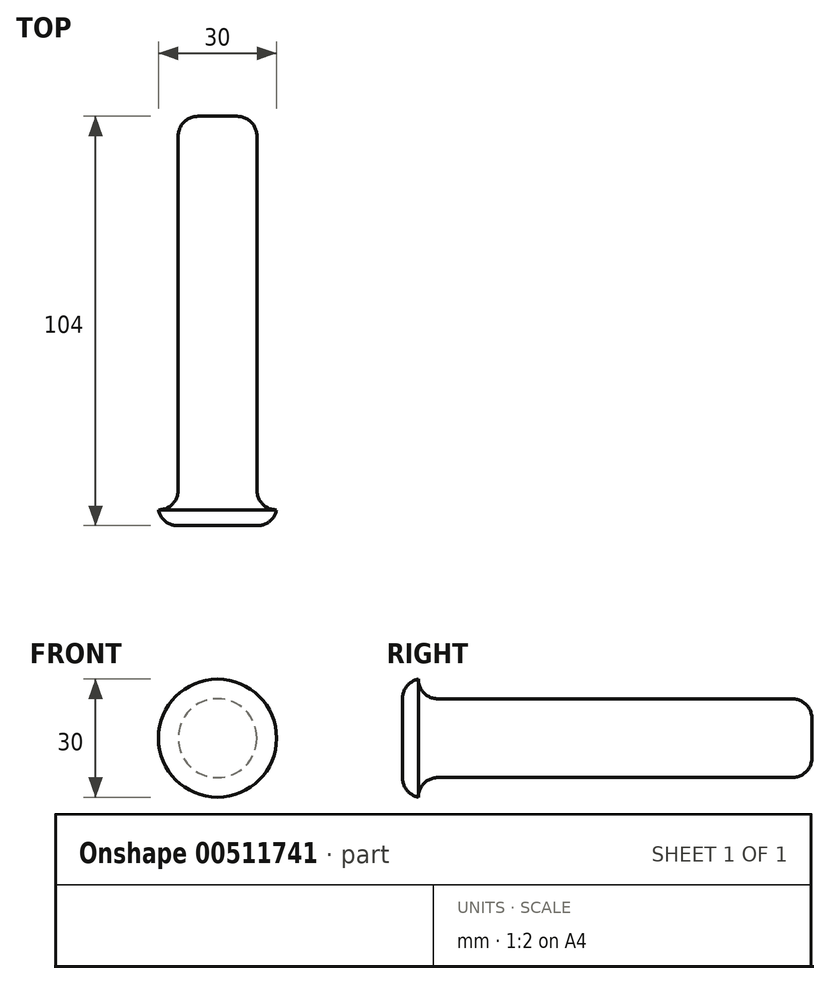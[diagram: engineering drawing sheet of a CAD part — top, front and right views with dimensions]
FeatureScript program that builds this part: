
annotation { "Feature Type Name" : "Feature", "Feature Type Description" : "" }
export const myFeature = defineFeature(function(context is Context, id is Id, definition is map)
    precondition{}
    {
        {
            var Q0;
            Q0=qCreatedBy(makeId("Front.planeOp"),FACE);
            var sketch = newSketch(context, id + "F0", { "sketchPlane" : qUnion([Q0])});
            skCircle(sketch, "E0", {"center": v(0, 0) * mm, "radius": 10 * mm});
            skCircle(sketch, "E1", {"center": v(0, 0) * mm, "radius": 20 * mm});
            skSolve(sketch);
        }
        {
            var Q0;
            Q0=makeQuery(id+"F0.imprint","IMPRINT",FACE,{"disambiguationData":[TD([[makeQuery(id+"F0.imprint","IMPRINT",EDGE,{"derivedFrom":sQuery(id+"F0.wireOp",EDGE,"E0")}),1.0]])]});
            extrude(context, id + "F1", {"entities" : qUnion([Q0]), "depth" : 104 * mm, "offsetDistance" : 25 * mm});
        }
        {
            var Q0;
            Q0=makeQuery(id+"F1.opExtrude","CAP_FACE",FACE,{"disambiguationData":[OSD([sQuery(id+"F0.wireOp",EDGE,"E0")])],"isStart":false});
            var sketch = newSketch(context, id + "F2", { "sketchPlane" : qUnion([Q0])});
            skCircle(sketch, "E2", {"center": v(0, 0) * mm, "radius": 15 * mm});
            skSolve(sketch);
        }
        {
            var Q0;
            Q0 = qSketchRegion(id + "F2", true);
            extrude(context, id + "F3", {"entities" : qUnion([Q0]), "operationType" : NewBodyOperationType.ADD, "oppositeDirection" : true, "depth" : 4 * mm, "offsetDistance" : 25 * mm});
        }
        {
            var Q0;
            Q0=makeQuery(id+"F3.boolean.opBoolean","INTERSECT",EDGE,{"derivedFrom":[makeQuery(id+"F1.opExtrude","SWEPT_FACE",FACE,{"disambiguationData":[OSD([sQuery(id+"F0.wireOp",EDGE,"E0")])]}),makeQuery(id+"F3.opExtrude","CAP_FACE",FACE,{"disambiguationData":[OSD([sQuery(id+"F2.wireOp",EDGE,"E2")])],"isStart":false})]});
            fillet(context, id + "F4", {"entities" : qUnion([Q0]), "radius" : 5 * mm, "tangentPropagation" : true, "allowEdgeOverflow" : false});
        }
        {
            var Q0;
            Q0=makeQuery(id+"F3.opExtrude","CAP_EDGE",EDGE,{"disambiguationData":[OSD([sQuery(id+"F2.wireOp",EDGE,"E2")])],"isStart":true});
            var Q1;
            Q1=makeQuery(id+"F1.opExtrude","CAP_EDGE",EDGE,{"disambiguationData":[OSD([sQuery(id+"F0.wireOp",EDGE,"E0")])],"isStart":true});
            fillet(context, id + "F5", {"entities" : qUnion([Q0, Q1]), "radius" : 5 * mm, "tangentPropagation" : true, "allowEdgeOverflow" : false});
        }
    });
